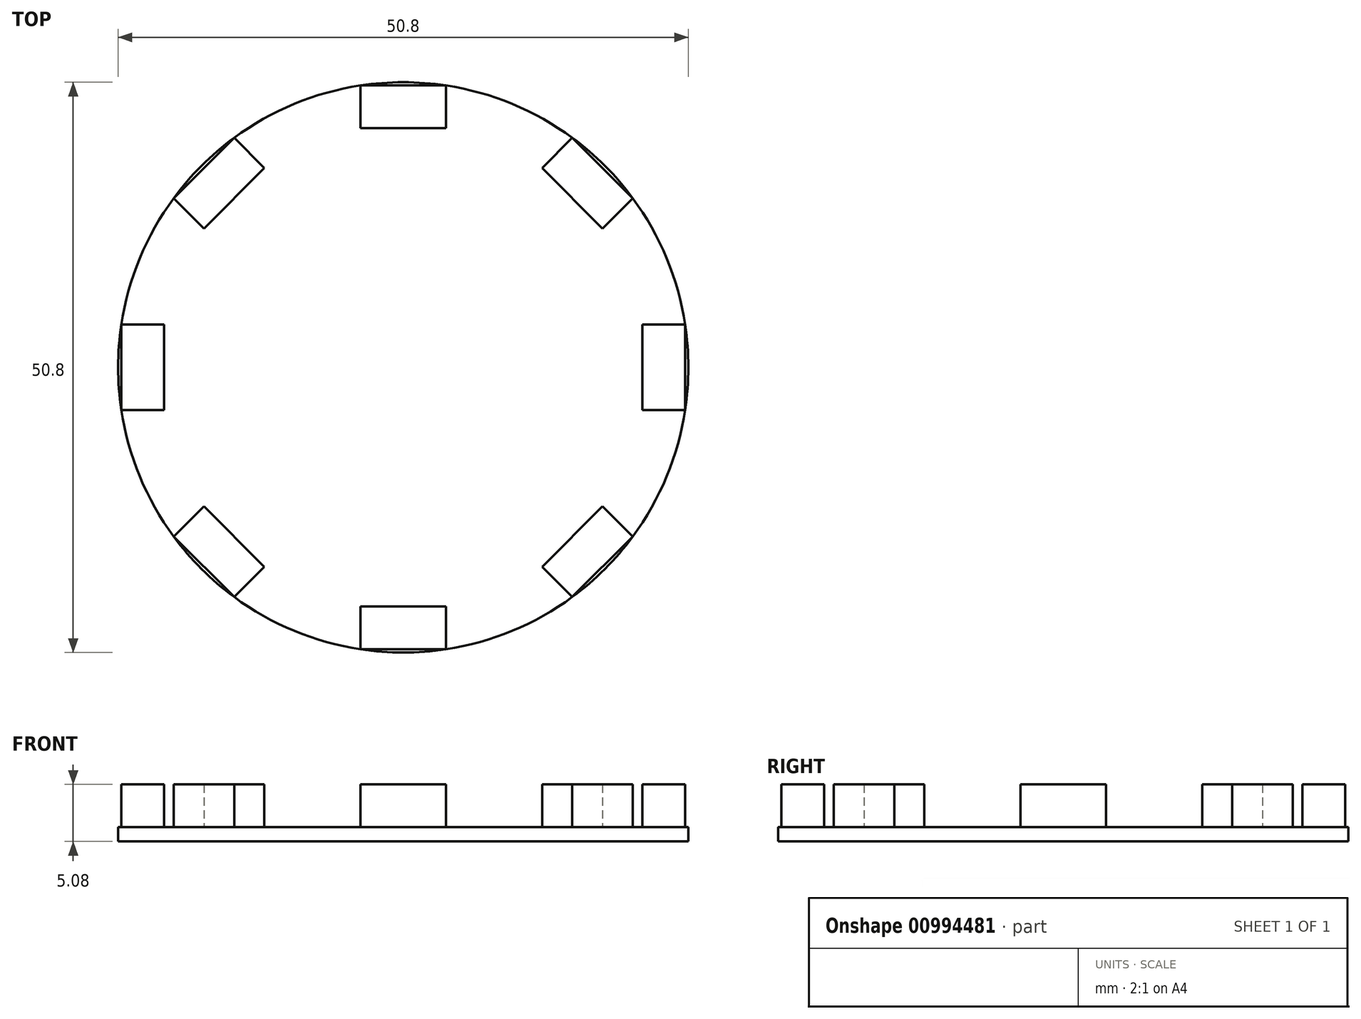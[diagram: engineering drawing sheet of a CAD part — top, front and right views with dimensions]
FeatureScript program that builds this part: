
annotation { "Feature Type Name" : "Feature", "Feature Type Description" : "" }
export const myFeature = defineFeature(function(context is Context, id is Id, definition is map)
    precondition{}
    {
        {
            var Q0;
            Q0=qCreatedBy(makeId("Top.planeOp"),FACE);
            var sketch = newSketch(context, id + "F0", { "sketchPlane" : qUnion([Q0])});
            skCircle(sketch, "E0", {"center": v(0, 0) * mm, "radius": 25.4 * mm});
            skSolve(sketch);
        }
        {
            var Q0;
            Q0 = qSketchRegion(id + "F0", true);
            extrude(context, id + "F1", {"entities" : qUnion([Q0]), "depth" : 1.27 * mm, "offsetDistance" : 25.4 * mm});
        }
        {
            var Q0;
            Q0=qCreatedBy(makeId("Top.planeOp"),FACE);
            var sketch = newSketch(context, id + "F2", { "sketchPlane" : qUnion([Q0])});
            skLineSegment(sketch, "E1.bottom", {"start": v(-25.11, 3.81) * mm, "end": v(-21.3, 3.81) * mm});
            skLineSegment(sketch, "E1.top", {"start": v(-25.11, -3.81) * mm, "end": v(-21.3, -3.81) * mm});
            skLineSegment(sketch, "E1.left", {"start": v(-25.11, 3.81) * mm, "end": v(-25.11, -3.81) * mm});
            skLineSegment(sketch, "E1.right", {"start": v(-21.3, 3.81) * mm, "end": v(-21.3, -3.81) * mm});
            skSolve(sketch);
        }
        {
            var Q0;
            Q0 = qSketchRegion(id + "F2", true);
            extrude(context, id + "F3", {"entities" : qUnion([Q0]), "operationType" : NewBodyOperationType.ADD, "depth" : 5.08 * mm, "offsetDistance" : 25.4 * mm});
        }
        {
            var Q0;
            Q0=makeQuery(id+"F1.opExtrude","SWEPT_BODY",BODY,{"disambiguationData":[OSD([sQuery(id+"F0.wireOp",EDGE,"E0")])]});
            var Q1;
            Q1=makeQuery(id+"F3.boolean.opBoolean","SPLIT",EDGE,{"disambiguationData":[OD(1.0)],"derivedFrom":makeQuery(id+"F1.opExtrude","CAP_EDGE",EDGE,{"disambiguationData":[OSD([sQuery(id+"F0.wireOp",EDGE,"E0")])],"isStart":false})});
            circularPattern(context, id + "F4", {"operationType" : NewBodyOperationType.ADD, "entities" : qUnion([Q0]), "axis" : qUnion([Q1]), "angle" : 360 * degree, "instanceCount" : 8, "equalSpace" : true});
        }
    });
